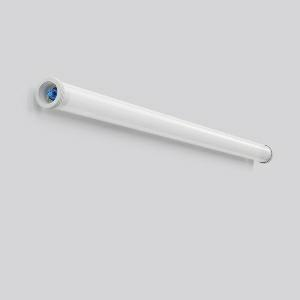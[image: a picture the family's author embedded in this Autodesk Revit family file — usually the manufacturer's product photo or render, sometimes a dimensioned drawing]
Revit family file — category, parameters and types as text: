
# Revit family: planox_tube_601072_002_730_1ea4
name_source: partatom
category: Lighting Fixtures
units: mm (PartAtom-declared; Revit-internal decimal feet)

## family parameters
Cut with Voids When Loaded = No
Host = Face
Light Source = No
Part Type = Normal
Room Calculation Point = No
Round Connector Dimension = Use Diameter
Shared = No

## types (1)
- PLANOX TUBE (1 x LED Modul 840, 8650 lm, 4000)
    Apparent Load = 62 VA
    CIE Flux Codes = 42 71 90 91 100
    Color Rendering = 80
    Color Temperature = 4000
    Default Elevation = 1800 mm
    Description = Series: PLANOX TUBE
Robust protective tube luminaire for tough requirements. Rack made of sheet steel, white powder coated. End caps made of plastic (polyamide) grey. Diffuser made of plastic (polycarbonate), opal, shockproof. Symmetrical light distribution. Homogeneous light distribution. With accessories for wall, ceiling or pendant mounting. Driver integrated.Easy installation with the Plug+Play Wieland RST CLASSIC plug-in system. With Casambi smart+free Bluetooth control for wireless network and operation using Android / iOS devices, free app available for download. Mounting set must be ordered separately. Luminaire with limited surface temperature in accordance with EN 60598-2-24 for use in environments in which a deposit of conductive dust on the luminaire can be expected. Qualified for use in the food and drink industry. Suitable for lighting in public car parks and public off-street parking spaces according to DIN 67528. Environmentally friendly and resource-saving due to replaceable components. 
Colour: white
Diameter: 78 mm
Length: 1564 mm
Lamp: LED
Socket: without socket
Colour temperature: 4000K
Colour rendering index (CRI): 83
System power: 62 W
Rated luminous flux: 8650 lm
Luminous efficiency: 140 lm/W
Control gear: Dimmable Bluetooth converter
Protection class: I
Type of protection: IP 67
    Height = 0 mm  [stored 0 ft]
    Lamp = 1 x LED Modul 840
    Lamp Light Flux = 8650 lm
    Lamp count = 1
    Length = 1564 mm
    Lifetime = 50000 h
    Luminous efficacy = 140 lm/W
    Manufacturer = RZB
    ModVariant = No
    Model = 601072.002.730
    Mounting Place = Ceiling
    Mounting Type = Surface mounted
    Number of Poles = 1
    OnlyDefault = Yes
    Power Factor = 1
    Product Name = PLANOX TUBE
    Product group = Surface mounted luminaires for moist/humid enviroments
    ProductGroupID = 308
    Protection Class = Protection class I
    Protection Degree = Degree of protection
    RLX_Detail_Level = 1
    RLX_Emergency_Light_Flux = 0 lm
    RLX_Emergency_Type = 0
    RLX_Emergency_Type_DB = No
    RlxData = <blob elided: 34821 chars, md5=738719fb>
    Socket = socket
    Standby Power = 0 W
    System Light Flux = 8650 lm
    System Power = 62 W
    Type Comments = Product without accessories
    Type Image = 601072.002.jpg
    URL = http://relux.com
    VarID = ---
    Voltage = 0 V
    Weight = 0.00 kg
    Width = 0 mm  [stored 0 ft]

note: [stored X ft] marks values corroborated as IEEE doubles in the binary element streams (Revit-internal decimal feet)

## geometry (parser evidence)
native form markers: Blend x4, Sweep x13
no freeform markers — native parametric forms only
